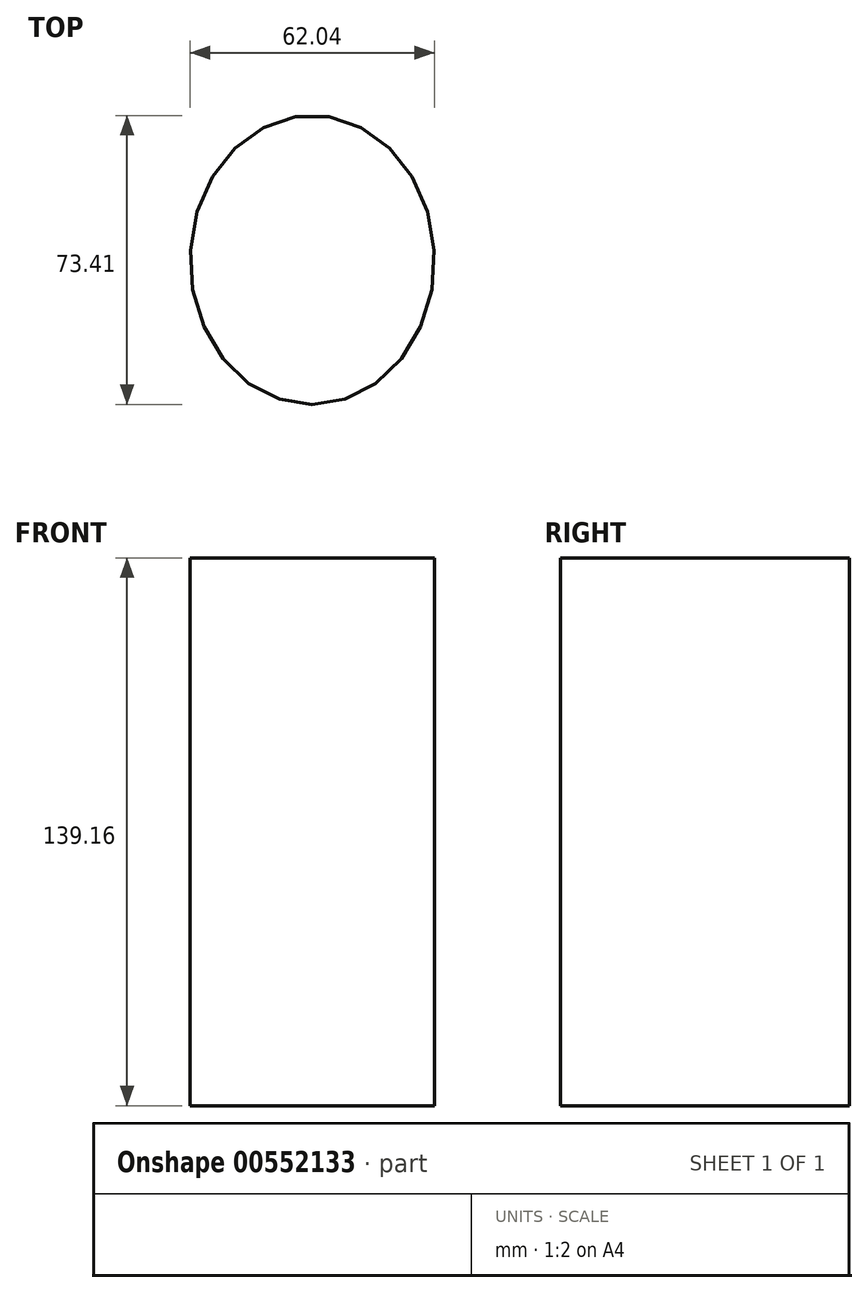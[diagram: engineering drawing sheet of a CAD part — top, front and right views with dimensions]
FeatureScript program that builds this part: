
annotation { "Feature Type Name" : "Feature", "Feature Type Description" : "" }
export const myFeature = defineFeature(function(context is Context, id is Id, definition is map)
    precondition{}
    {
        {
            var Q0;
            Q0=qCreatedBy(makeId("Top.planeOp"),FACE);
            var sketch = newSketch(context, id + "F0", { "sketchPlane" : qUnion([Q0])});
            skEllipse(sketch, "E0", {"center": v(0, -3.4) * mm, "majorRadius": 36.7 * mm, "minorRadius": 31.02 * mm, "majorAxis": v(0, -1)});
            skEllipse(sketch, "E1", {"center": v(-31.62, -40.99) * mm, "majorRadius": 14.17 * mm, "minorRadius": 14.93 * mm, "majorAxis": v(1, 0)});
            skSolve(sketch);
        }
        {
            var Q0;
            Q0=makeQuery(id+"F0.imprint","IMPRINT",FACE,{"disambiguationData":[TD([[makeQuery(id+"F0.imprint","IMPRINT",EDGE,{"derivedFrom":sQuery(id+"F0.wireOp",EDGE,"E0")}),1.0]])]});
            extrude(context, id + "F1", {"entities" : qUnion([Q0]), "depth" : 139.16 * mm, "offsetDistance" : 25.4 * mm});
        }
    });
